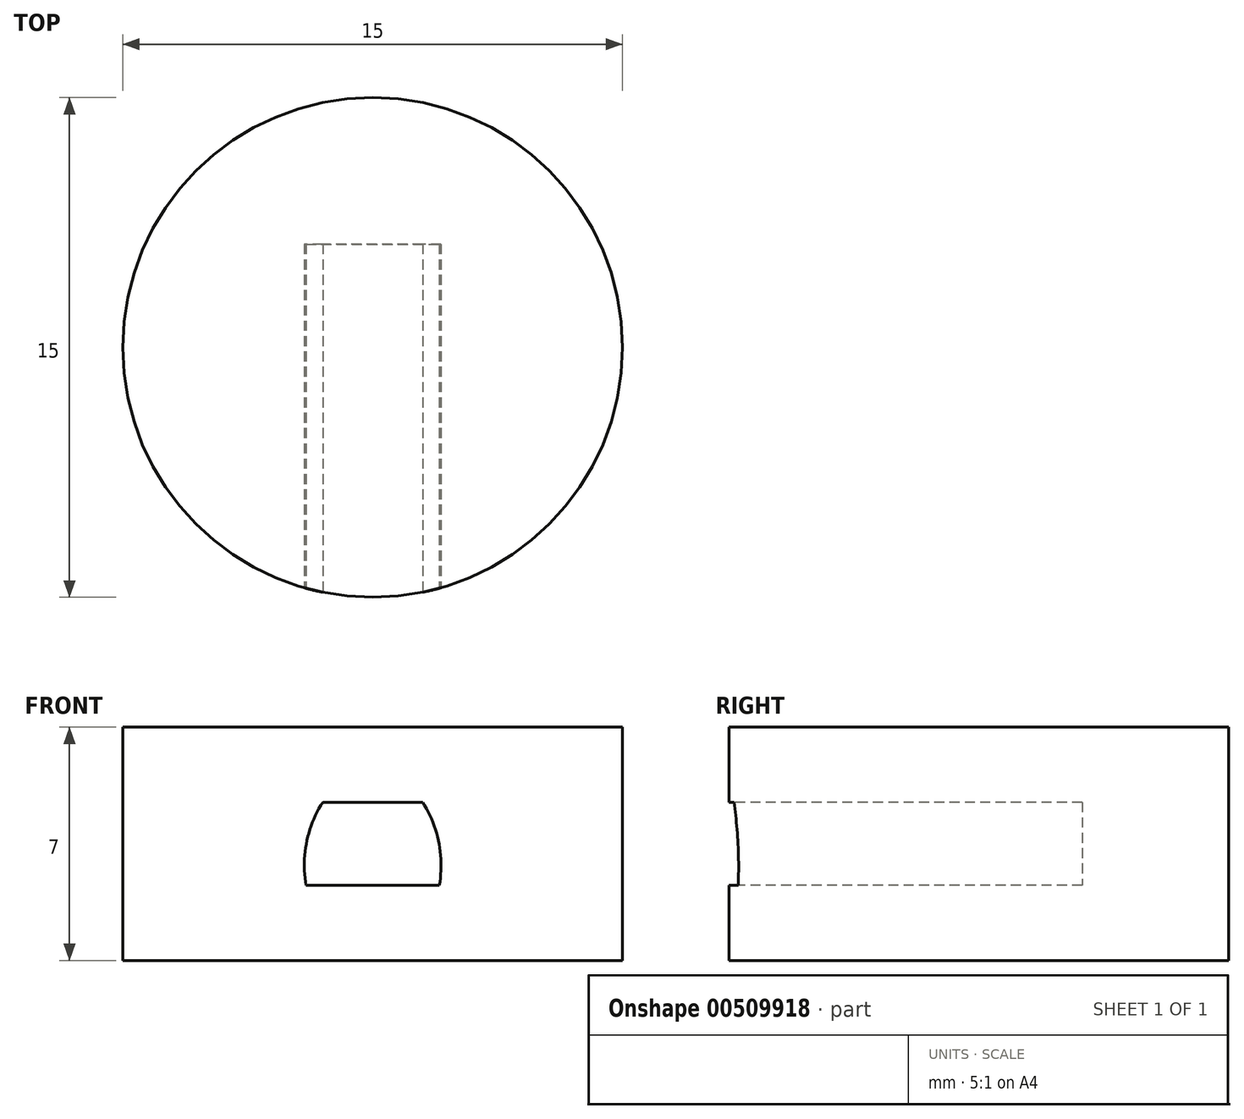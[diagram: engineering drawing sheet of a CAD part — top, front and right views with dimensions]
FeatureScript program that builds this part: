
annotation { "Feature Type Name" : "Feature", "Feature Type Description" : "" }
export const myFeature = defineFeature(function(context is Context, id is Id, definition is map)
    precondition{}
    {
        {
            var Q0;
            Q0=qCreatedBy(makeId("Top.planeOp"),FACE);
            var sketch = newSketch(context, id + "F0", { "sketchPlane" : qUnion([Q0])});
            skLineSegment(sketch, "E0.bottom", {"start": v(7.5, -7.5) * mm, "end": v(-7.5, -7.5) * mm});
            skLineSegment(sketch, "E0.top", {"start": v(7.5, 7.5) * mm, "end": v(-7.5, 7.5) * mm});
            skLineSegment(sketch, "E0.left", {"start": v(7.5, -7.5) * mm, "end": v(7.5, 7.5) * mm});
            skLineSegment(sketch, "E0.right", {"start": v(-7.5, -7.5) * mm, "end": v(-7.5, 7.5) * mm});
            skPoint(sketch, "E0.middle", {"position": v(0, 0) * mm});
            skSolve(sketch);
        }
        {
            var Q0;
            Q0 = qSketchRegion(id + "F0", true);
            extrude(context, id + "F1", {"entities" : qUnion([Q0]), "depth" : 7 * mm});
        }
        {
            var Q0;
            Q0=makeQuery(id+"F1.opExtrude","SWEPT_FACE",FACE,{"disambiguationData":[OSD([sQuery(id+"F0.wireOp",EDGE,"E0.bottom")])]});
            var sketch = newSketch(context, id + "F2", { "sketchPlane" : qUnion([Q0])});
            skLineSegment(sketch, "E1", {"start": v(-7.5, 3.5) * mm, "end": v(7.5, 3.5) * mm, "construction": true});
            skLineSegment(sketch, "E2.top", {"start": v(1.5, 4.75) * mm, "end": v(-1.5, 4.75) * mm});
            skPoint(sketch, "E2.middle", {"position": v(0, 3.5) * mm});
            skPoint(sketch, "E3.orphan", {"position": v(2, 4.75) * mm});
            skPoint(sketch, "E4.orphan", {"position": v(-2, 4.75) * mm});
            skPoint(sketch, "E5.bottom.start.orphan", {"position": v(1.5, 2.25) * mm});
            skPoint(sketch, "E2.bottom.end.orphan", {"position": v(-1.5, 2.25) * mm});
            skLineSegment(sketch, "E6", {"start": v(-2, 2.25) * mm, "end": v(2, 2.25) * mm});
            skArc(sketch, "E7", {"start": v(-1.5, 4.75) * mm, "mid": v(-1.99, 3.55) * mm, "end": v(-2, 2.25) * mm});
            skLineSegment(sketch, "E8", {"start": v(0, 4.75) * mm, "end": v(0, 2.25) * mm, "construction": true});
            skArc(sketch, "E9.MirrorCS", {"start": v(1.5, 4.75) * mm, "mid": v(1.99, 3.55) * mm, "end": v(2, 2.25) * mm});
            skSolve(sketch);
        }
        {
            var Q0;
            Q0 = qSketchRegion(id + "F2", true);
            extrude(context, id + "F3", {"entities" : qUnion([Q0]), "operationType" : NewBodyOperationType.REMOVE, "oppositeDirection" : true, "depth" : 10.6 * mm});
        }
        {
            var Q0;
            Q0=makeQuery(id+"F1.opExtrude","SWEPT_EDGE",EDGE,{"disambiguationData":[OSD([sQuery(id+"F0.wireOp",EDGE,"E0.bottom"),sQuery(id+"F0.wireOp",EDGE,"E0.right")])]});
            var Q1;
            Q1=makeQuery(id+"F1.opExtrude","SWEPT_EDGE",EDGE,{"disambiguationData":[OSD([sQuery(id+"F0.wireOp",EDGE,"E0.bottom"),sQuery(id+"F0.wireOp",EDGE,"E0.left")])]});
            var Q2;
            Q2=makeQuery(id+"F1.opExtrude","SWEPT_EDGE",EDGE,{"disambiguationData":[OSD([sQuery(id+"F0.wireOp",EDGE,"E0.top"),sQuery(id+"F0.wireOp",EDGE,"E0.left")])]});
            var Q3;
            Q3=makeQuery(id+"F1.opExtrude","SWEPT_EDGE",EDGE,{"disambiguationData":[OSD([sQuery(id+"F0.wireOp",EDGE,"E0.top"),sQuery(id+"F0.wireOp",EDGE,"E0.right")])]});
            fillet(context, id + "F4", {"entities" : qUnion([Q0, Q1, Q2, Q3]), "radius" : 7.5 * mm, "tangentPropagation" : true, "allowEdgeOverflow" : false});
        }
    });
